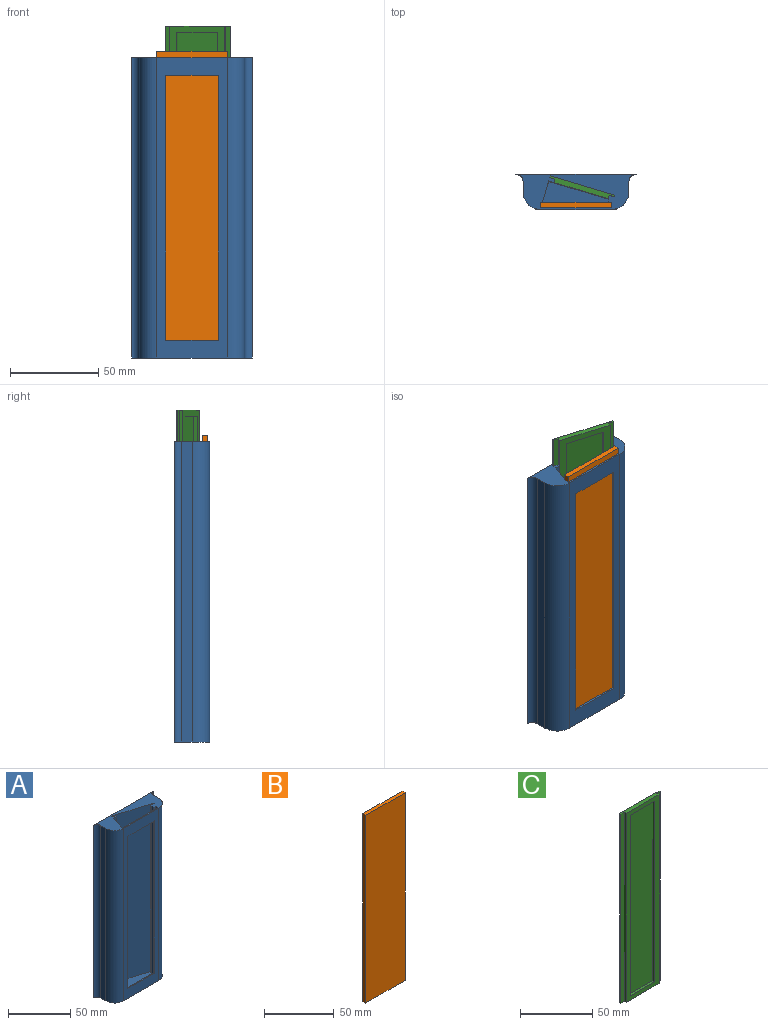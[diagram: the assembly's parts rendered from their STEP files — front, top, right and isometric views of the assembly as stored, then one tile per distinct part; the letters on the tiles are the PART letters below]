
ASSEMBLY  parts=3 mates=3
PART A: 30 faces, bbox 68x20x170 mm
  f0: plane 170x40mm, normal (0,-1,0), area 2300mm2, adj f2,f8,f9,f10,f26,f27,f28,f29
  f1: plane 165x40mm, normal (0,1,0), area 2100mm2, adj f2,f11,f24,f25,f26,f27,f28,f29
  f2: plane 68x20mm, normal (0,0,1), area 680.9mm2, adj f0,f1,f3,f4,f5,f6,f7,f8
  f3: plane 170x6mm, normal (1,0,0), area 1020mm2, adj f2,f4,f9,f10
  f4: cylinder r=4mm len=170mm, axis (0,0,1), area 1068.1mm2, adj f2,f3,f5,f10
  f5: plane 170x68mm, normal (0,1,0), area 11560mm2, adj f2,f4,f6,f10
  f6: cylinder r=4mm len=170mm, axis (0,0,1), area 1068.1mm2, adj f2,f5,f7,f10
  f7: plane 170x6mm, normal (-1,0,0), area 1020mm2, adj f2,f6,f8,f10
  f8: cylinder r=10mm len=170mm, axis (0,0,1), area 2670.4mm2, adj f0,f2,f7,f10
  f9: cylinder r=10mm len=170mm, axis (0,0,1), area 2670.4mm2, adj f0,f2,f3,f10
  f10: plane 68x20mm, normal (0,0,-1), area 1163.9mm2, adj f0,f3,f4,f5,f6,f7,f8,f9
  f11: plane 165x3mm, normal (-1,0,0), area 495mm2, adj f1,f2,f12,f25
  f12: plane 165x1.71mm, normal (0,-1,0), area 281.4mm2, adj f2,f11,f13,f25
  f13: plane 165x2mm, normal (-1,0,0), area 330mm2, adj f2,f12,f14,f25
  f14: plane 165x1.92mm, normal (-0.96,0.29,0), area 330mm2, adj f2,f13,f15,f25
  f15: plane 165x2.87mm, normal (0.29,0.96,0), area 495mm2, adj f2,f14,f16,f25
  f16: plane 165x0.96mm, normal (-0.96,0.29,0), area 165mm2, adj f2,f15,f17,f25
  f17: plane 165x36.56mm, normal (-0.29,-0.96,0), area 6298.4mm2, adj f2,f16,f18,f25
  f18: plane 165x0.96mm, normal (0.96,-0.29,0), area 165mm2, adj f2,f17,f19,f25
  f19: plane 165x2.87mm, normal (0.29,0.96,0), area 495mm2, adj f2,f18,f20,f25
  f20: plane 165x1.92mm, normal (0.96,-0.29,0), area 330mm2, adj f2,f19,f21,f25
  f21: plane 165x2.94mm, normal (-0.29,-0.96,0), area 506.6mm2, adj f2,f20,f22,f25
  f22: plane 165x12.13mm, normal (0.96,-0.29,0), area 2089.1mm2, adj f2,f21,f23,f25
  f23: plane 165x0.9mm, normal (0,-1,0), area 148.5mm2, adj f2,f22,f24,f25
  f24: plane 165x3mm, normal (1,0,0), area 495mm2, adj f1,f2,f23,f25
  f25: plane 42.03x17.98mm, normal (0,0,1), area 483mm2, adj f1,f11,f12,f13,f14,f15,f16,f17
  f26: plane 30x1mm, normal (0,0,-1), area 30mm2, adj f0,f1,f27,f29
  f27: plane 150x1mm, normal (1,0,0), area 150mm2, adj f0,f1,f26,f28
  f28: plane 30x1mm, normal (0,0,1), area 30mm2, adj f0,f1,f27,f29
  f29: plane 150x1mm, normal (-1,0,0), area 150mm2, adj f0,f1,f26,f28
PART B: 6 faces, bbox 40x3x165 mm
  f0: plane 165x40mm, normal (0,1,0), area 6600mm2, adj f1,f3,f4,f5
  f1: plane 165x3mm, normal (-1,0,0), area 495mm2, adj f0,f2,f4,f5
  f2: plane 165x40mm, normal (0,-1,0), area 6600mm2, adj f1,f3,f4,f5
  f3: plane 165x3mm, normal (1,0,0), area 495mm2, adj f0,f2,f4,f5
  f4: plane 40x3mm, normal (0,0,-1), area 120mm2, adj f0,f1,f2,f3
  f5: plane 40x3mm, normal (0,0,1), area 120mm2, adj f0,f1,f2,f3
PART C: 15 faces, bbox 38.2x3x160 mm
  f0: plane 160x32.17mm, normal (0,-1,0), area 1455.9mm2, adj f1,f7,f8,f9,f10,f11,f12,f13
  f1: plane 160x2mm, normal (1,0,0), area 320mm2, adj f0,f2,f8,f9
  f2: plane 160x3mm, normal (0,-1,0), area 480mm2, adj f1,f3,f8,f9
  f3: plane 160x1mm, normal (1,0,0), area 160mm2, adj f2,f4,f8,f9
  f4: plane 160x38.17mm, normal (0,1,0), area 6107.5mm2, adj f3,f5,f8,f9
  f5: plane 160x1mm, normal (-1,0,0), area 160mm2, adj f4,f6,f8,f9
  f6: plane 160x3mm, normal (0,-1,0), area 480mm2, adj f5,f7,f8,f9
  f7: plane 160x2mm, normal (-1,0,0), area 320mm2, adj f0,f6,f8,f9
  f8: plane 38.17x3mm, normal (0,0,-1), area 102.5mm2, adj f0,f1,f2,f3,f4,f5,f6,f7
  f9: plane 38.17x3mm, normal (0,0,1), area 102.5mm2, adj f0,f1,f2,f3,f4,f5,f6,f7
  f10: plane 152.99x2mm, normal (-1,0,0), area 306mm2, adj f0,f11,f13,f14
  f11: plane 24.13x2mm, normal (0,0,-1), area 48.3mm2, adj f0,f10,f12,f14
  f12: plane 152.99x2mm, normal (1,0,0), area 306mm2, adj f0,f11,f13,f14
  f13: plane 24.13x2mm, normal (0,0,1), area 48.3mm2, adj f0,f10,f12,f14
  f14: plane 152.99x24.13mm, normal (0,-1,0), area 3691.6mm2, adj f10,f11,f12,f13
PLACE A t=(-43.75,16.79,28.82)mm
PLACE B t=(-63.75,0.79,32.46)mm
PLACE C rot(axis=(0,0,-1),16.7deg) t=(-35.22,3.06,46.74)mm
MATE planar C.f3 <-> A.f16  axis (0.96,-0.29,0) through (-21.87,4.32,-33.26)mm
MATE planar B.f1 <-> A.f24  axis (-1,0,0) through (-63.75,-0.71,32.46)mm
MATE planar C.f4 <-> A.f17  axis (0.29,0.96,0) through (-40,10.28,-33.26)mm
